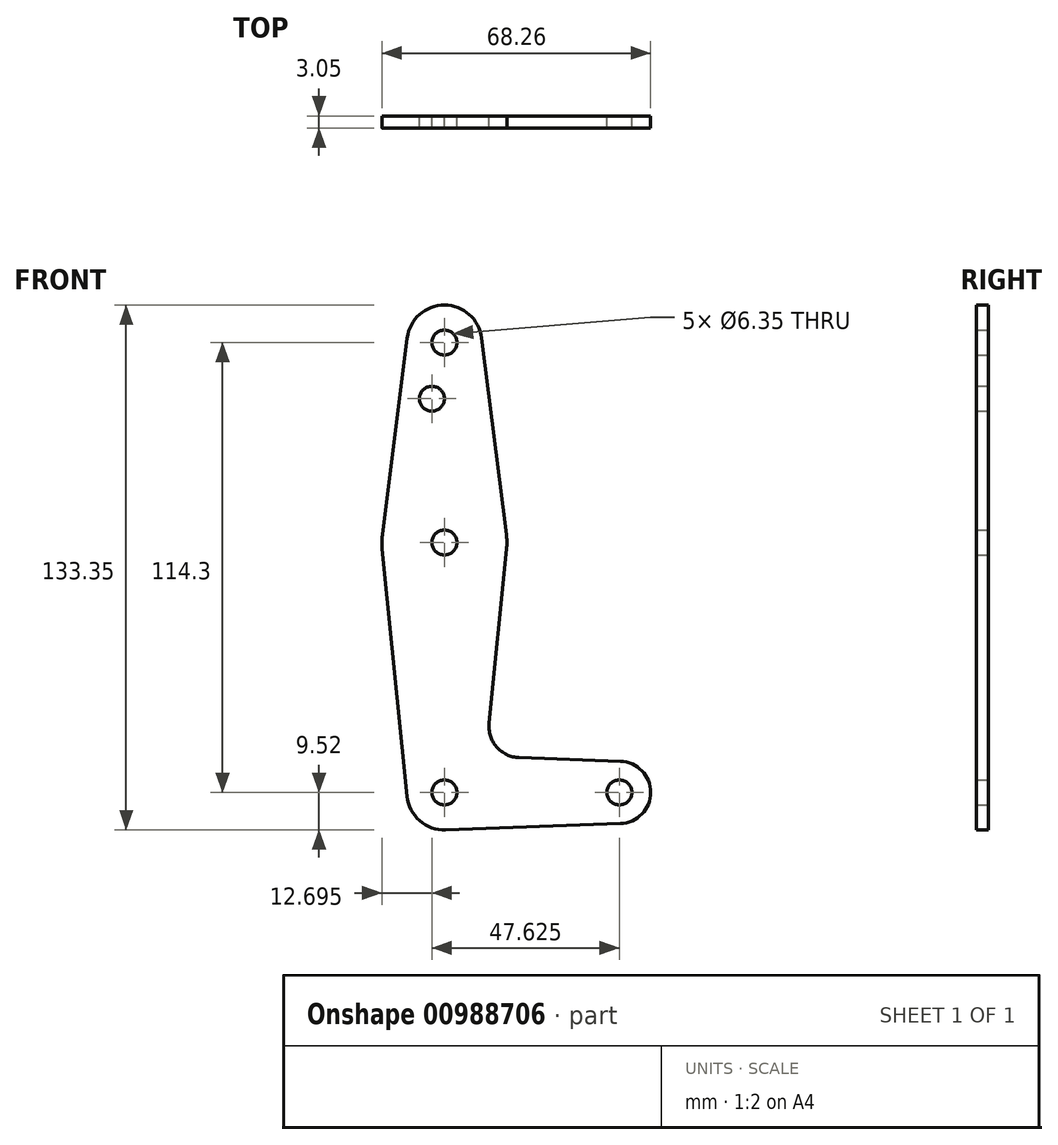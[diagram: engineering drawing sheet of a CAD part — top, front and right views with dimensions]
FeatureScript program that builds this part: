
annotation { "Feature Type Name" : "Feature", "Feature Type Description" : "" }
export const myFeature = defineFeature(function(context is Context, id is Id, definition is map)
    precondition{}
    {
        {
            var Q0;
            Q0=qCreatedBy(makeId("Front.planeOp"),FACE);
            var sketch = newSketch(context, id + "F0", { "sketchPlane" : qUnion([Q0])});
            skLineSegment(sketch, "E0", {"start": v(0, 0) * mm, "end": v(0, 114.3) * mm, "construction": true});
            skLineSegment(sketch, "E1", {"start": v(0, 0) * mm, "end": v(44.45, 0) * mm, "construction": true});
            skCircle(sketch, "E2", {"center": v(0, 114.3) * mm, "radius": 9.53 * mm});
            skCircle(sketch, "E3", {"center": v(0, 63.5) * mm, "radius": 15.88 * mm});
            skCircle(sketch, "E4", {"center": v(0, 0) * mm, "radius": 9.53 * mm});
            skCircle(sketch, "E5", {"center": v(44.45, 0) * mm, "radius": 7.94 * mm});
            skLineSegment(sketch, "E6", {"start": v(-9.45, 115.5) * mm, "end": v(-15.75, 65.48) * mm});
            skLineSegment(sketch, "E7", {"start": v(9.45, 115.5) * mm, "end": v(15.75, 65.48) * mm});
            skLineSegment(sketch, "E8", {"start": v(-9.48, -0.95) * mm, "end": v(-15.8, 61.91) * mm});
            skLineSegment(sketch, "E9", {"start": v(15.8, 61.91) * mm, "end": v(11.34, 17.6) * mm});
            skLineSegment(sketch, "E10", {"start": v(18.97, 8.85) * mm, "end": v(44.73, 7.93) * mm});
            skLineSegment(sketch, "E11", {"start": v(0.34, -9.52) * mm, "end": v(44.73, -7.93) * mm});
            skCircle(sketch, "E12", {"center": v(0, 114.3) * mm, "radius": 3.18 * mm});
            skCircle(sketch, "E13", {"center": v(-3.18, 100.03) * mm, "radius": 3.18 * mm});
            skCircle(sketch, "E14", {"center": v(0, 63.5) * mm, "radius": 3.18 * mm});
            skCircle(sketch, "E15", {"center": v(0, 0) * mm, "radius": 3.18 * mm});
            skCircle(sketch, "E16", {"center": v(44.45, 0) * mm, "radius": 3.18 * mm});
            skArc(sketch, "E17.filletArc", {"start": v(11.34, 17.6) * mm, "mid": v(13.26, 11.57) * mm, "end": v(18.97, 8.85) * mm});
            skSolve(sketch);
        }
        {
            var Q0;
            Q0=makeQuery(id+"F0.imprint","IMPRINT",FACE,{"disambiguationData":[TD([[makeQuery(id+"F0.imprint","IMPRINT",EDGE,{"derivedFrom":sQuery(id+"F0.wireOp",EDGE,"E12")}),-1.0]])]});
            var Q1;
            {var subQ0=sQuery(id+"F0.wireOp",EDGE,"E6");Q1=makeQuery(id+"F0.imprint","IMPRINT",FACE,{"disambiguationData":[TD([[makeQuery(id+"F0.imprint","IMPRINT",EDGE,{"derivedFrom":subQ0}),1.0]])]});}
            var Q2;
            Q2=makeQuery(id+"F0.imprint","IMPRINT",FACE,{"disambiguationData":[TD([[makeQuery(id+"F0.imprint","IMPRINT",EDGE,{"derivedFrom":sQuery(id+"F0.wireOp",EDGE,"E14")}),-1.0]])]});
            var Q3;
            {var subQ3=sQuery(id+"F0.wireOp",EDGE,"E8");Q3=makeQuery(id+"F0.imprint","IMPRINT",FACE,{"disambiguationData":[TD([[makeQuery(id+"F0.imprint","IMPRINT",EDGE,{"derivedFrom":subQ3}),-1.0]])]});}
            var Q4;
            Q4=makeQuery(id+"F0.imprint","IMPRINT",FACE,{"disambiguationData":[TD([[makeQuery(id+"F0.imprint","IMPRINT",EDGE,{"derivedFrom":sQuery(id+"F0.wireOp",EDGE,"E15")}),-1.0]])]});
            var Q5;
            Q5=makeQuery(id+"F0.imprint","IMPRINT",FACE,{"disambiguationData":[TD([[makeQuery(id+"F0.imprint","IMPRINT",EDGE,{"derivedFrom":sQuery(id+"F0.wireOp",EDGE,"E16")}),-1.0]])]});
            extrude(context, id + "F1", {"entities" : qUnion([Q0, Q1, Q2, Q3, Q4, Q5]), "depth" : 3.05 * mm, "offsetDistance" : 25.4 * mm});
        }
    });
